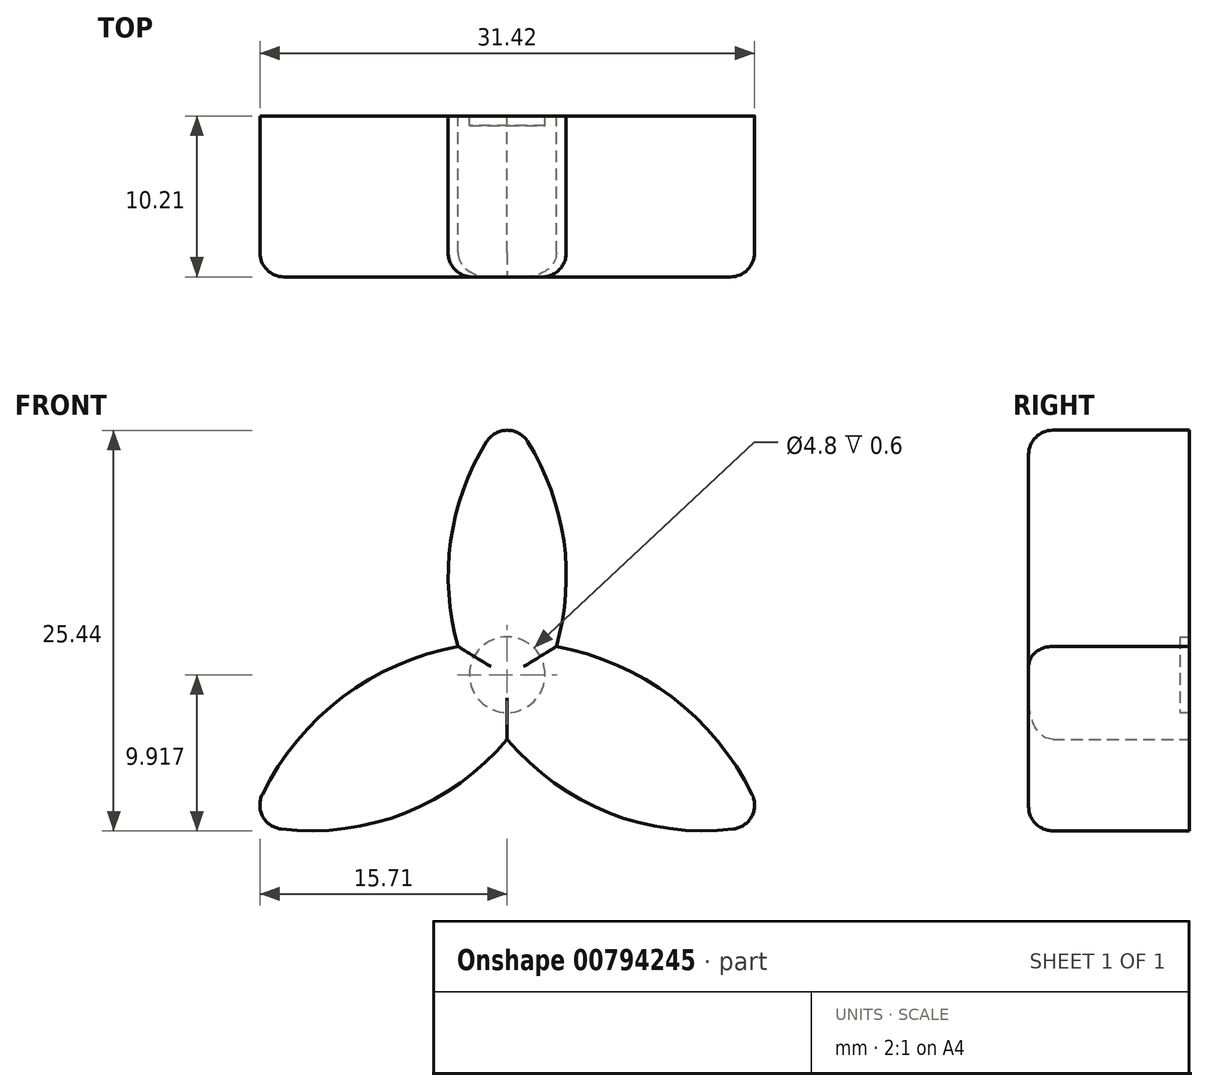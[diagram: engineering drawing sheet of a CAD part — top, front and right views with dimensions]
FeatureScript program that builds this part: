
annotation { "Feature Type Name" : "Feature", "Feature Type Description" : "" }
export const myFeature = defineFeature(function(context is Context, id is Id, definition is map)
    precondition{}
    {
        {
            var Q0;
            Q0=qCreatedBy(makeId("Front.planeOp"),FACE);
            var sketch = newSketch(context, id + "F0", { "sketchPlane" : qUnion([Q0])});
            skLineSegment(sketch, "E0", {"start": v(-12.42, 0) * mm, "end": v(0, 0) * mm});
            skLineSegment(sketch, "E1", {"start": v(0, 0) * mm, "end": v(12.42, 0) * mm});
            skLineSegment(sketch, "E2", {"start": v(0, 0) * mm, "end": v(0, -21.51) * mm});
            skLineSegment(sketch, "E3", {"start": v(-12.42, 0) * mm, "end": v(0, -21.51) * mm});
            skLineSegment(sketch, "E4", {"start": v(12.42, 0) * mm, "end": v(0, -21.51) * mm});
            skCircle(sketch, "E5", {"center": v(-12.42, 0) * mm, "radius": 16.17 * mm});
            skCircle(sketch, "E6", {"center": v(0, -21.51) * mm, "radius": 17.34 * mm});
            skCircle(sketch, "E7", {"center": v(12.42, 0) * mm, "radius": 16.17 * mm});
            skSolve(sketch);
        }
        {
            var Q0;
            {var subQ0=sQuery(id+"F0.wireOp",EDGE,"E6");var subQ1=sQuery(id+"F0.wireOp",EDGE,"E3");var subQ2=makeQuery(id+"F0.imprint","INTERSECT",VERTEX,{"derivedFrom":[subQ1,subQ0]});Q0=makeQuery(id+"F0.imprint","IMPRINT",FACE,{"disambiguationData":[TD([[makeQuery(id+"F0.imprint","IMPRINT",EDGE,{"disambiguationData":[TD([[subQ2,-1.0]])],"derivedFrom":subQ1}),-1.0]])]});}
            var Q1;
            {var subQ0=sQuery(id+"F0.wireOp",EDGE,"E6");var subQ1=sQuery(id+"F0.wireOp",EDGE,"E4");var subQ2=makeQuery(id+"F0.imprint","INTERSECT",VERTEX,{"derivedFrom":[subQ1,subQ0]});Q1=makeQuery(id+"F0.imprint","IMPRINT",FACE,{"disambiguationData":[TD([[makeQuery(id+"F0.imprint","IMPRINT",EDGE,{"disambiguationData":[TD([[subQ2,-1.0]])],"derivedFrom":subQ1}),1.0]])]});}
            var Q2;
            {var subQ0=sQuery(id+"F0.wireOp",EDGE,"E6");var subQ1=sQuery(id+"F0.wireOp",EDGE,"E3");var subQ2=makeQuery(id+"F0.imprint","INTERSECT",VERTEX,{"derivedFrom":[subQ1,subQ0]});Q2=makeQuery(id+"F0.imprint","IMPRINT",FACE,{"disambiguationData":[TD([[makeQuery(id+"F0.imprint","IMPRINT",EDGE,{"disambiguationData":[TD([[subQ2,-1.0]])],"derivedFrom":subQ1}),1.0]])]});}
            var Q3;
            {var subQ0=sQuery(id+"F0.wireOp",EDGE,"E6");var subQ1=sQuery(id+"F0.wireOp",EDGE,"E2");var subQ2=makeQuery(id+"F0.imprint","INTERSECT",VERTEX,{"derivedFrom":[subQ1,subQ0]});Q3=makeQuery(id+"F0.imprint","IMPRINT",FACE,{"disambiguationData":[TD([[makeQuery(id+"F0.imprint","IMPRINT",EDGE,{"disambiguationData":[TD([[subQ2,1.0]])],"derivedFrom":subQ0}),1.0]])]});}
            var Q4;
            {var subQ0=sQuery(id+"F0.wireOp",EDGE,"E6");var subQ1=sQuery(id+"F0.wireOp",EDGE,"E4");var subQ2=makeQuery(id+"F0.imprint","INTERSECT",VERTEX,{"derivedFrom":[subQ1,subQ0]});Q4=makeQuery(id+"F0.imprint","IMPRINT",FACE,{"disambiguationData":[TD([[makeQuery(id+"F0.imprint","IMPRINT",EDGE,{"disambiguationData":[TD([[subQ2,-1.0]])],"derivedFrom":subQ1}),-1.0]])]});}
            var Q5;
            {var subQ0=sQuery(id+"F0.wireOp",EDGE,"E6");var subQ1=sQuery(id+"F0.wireOp",EDGE,"E2");var subQ2=makeQuery(id+"F0.imprint","INTERSECT",VERTEX,{"derivedFrom":[subQ1,subQ0]});Q5=makeQuery(id+"F0.imprint","IMPRINT",FACE,{"disambiguationData":[TD([[makeQuery(id+"F0.imprint","IMPRINT",EDGE,{"disambiguationData":[TD([[subQ2,-1.0]])],"derivedFrom":subQ0}),1.0]])]});}
            var Q6;
            {var subQ0=sQuery(id+"F0.wireOp",EDGE,"E2");var subQ5=sQuery(id+"F0.wireOp",EDGE,"E6");var subQ6=makeQuery(id+"F0.imprint","INTERSECT",VERTEX,{"derivedFrom":[subQ0,subQ5]});Q6=makeQuery(id+"F0.imprint","IMPRINT",FACE,{"disambiguationData":[TD([[makeQuery(id+"F0.imprint","IMPRINT",EDGE,{"disambiguationData":[TD([[subQ6,-1.0]])],"derivedFrom":subQ5}),-1.0]])]});}
            var Q7;
            {var subQ1=sQuery(id+"F0.wireOp",EDGE,"E1");var subQ3=sQuery(id+"F0.wireOp",EDGE,"E5");var subQ4=makeQuery(id+"F0.imprint","INTERSECT",VERTEX,{"derivedFrom":[subQ1,subQ3]});Q7=makeQuery(id+"F0.imprint","IMPRINT",FACE,{"disambiguationData":[TD([[makeQuery(id+"F0.imprint","IMPRINT",EDGE,{"disambiguationData":[TD([[subQ4,1.0]])],"derivedFrom":subQ3}),1.0]])]});}
            var Q8;
            {var subQ3=sQuery(id+"F0.wireOp",EDGE,"E7");var subQ5=sQuery(id+"F0.wireOp",EDGE,"E5");var subQ6=makeQuery(id+"F0.imprint","INTERSECT",VERTEX,{"derivedFrom":[subQ5,subQ3]});Q8=makeQuery(id+"F0.imprint","IMPRINT",FACE,{"disambiguationData":[TD([[makeQuery(id+"F0.imprint","IMPRINT",EDGE,{"disambiguationData":[TD([[subQ6,1.0]])],"derivedFrom":subQ5}),1.0]])]});}
            extrude(context, id + "F1", {"entities" : qUnion([Q0, Q1, Q2, Q3, Q4, Q5, Q6, Q7, Q8]), "depth" : 19.91 * mm, "offsetDistance" : 25.4 * mm});
        }
        {
            var Q0;
            {var subQ0=sQuery(id+"F0.wireOp",EDGE,"E5");var subQ1=makeQuery(id+"F0.imprint","INTERSECT",VERTEX,{"derivedFrom":[sQuery(id+"F0.wireOp",EDGE,"E3"),subQ0]});Q0=makeQuery(id+"F1.opExtrude","CAP_EDGE",EDGE,{"disambiguationData":[OSD([subQ0]),TDD([makeQuery(id+"F0.imprint","IMPRINT",EDGE,{"disambiguationData":[TD([[makeQuery(id+"F0.imprint","INTERSECT",VERTEX,{"disambiguationData":[OD(0.0)],"derivedFrom":[subQ0,sQuery(id+"F0.wireOp",EDGE,"E6")]}),-1.0]])],"derivedFrom":subQ0}),makeQuery(id+"F0.imprint","IMPRINT",EDGE,{"disambiguationData":[TD([[subQ1,-1.0]])],"derivedFrom":subQ0})])],"isStart":false});}
            var Q1;
            {var subQ0=sQuery(id+"F0.wireOp",EDGE,"E6");var subQ1=makeQuery(id+"F0.imprint","INTERSECT",VERTEX,{"derivedFrom":[sQuery(id+"F0.wireOp",EDGE,"E3"),subQ0]});Q1=makeQuery(id+"F1.opExtrude","CAP_EDGE",EDGE,{"disambiguationData":[OSD([subQ0]),TDD([makeQuery(id+"F0.imprint","IMPRINT",EDGE,{"disambiguationData":[TD([[subQ1,1.0]])],"derivedFrom":subQ0}),makeQuery(id+"F0.imprint","IMPRINT",EDGE,{"disambiguationData":[TD([[makeQuery(id+"F0.imprint","INTERSECT",VERTEX,{"disambiguationData":[OD(0.0)],"derivedFrom":[sQuery(id+"F0.wireOp",EDGE,"E5"),subQ0]}),1.0]])],"derivedFrom":subQ0})])],"isStart":false});}
            var Q2;
            {var subQ0=sQuery(id+"F0.wireOp",EDGE,"E7");var subQ1=makeQuery(id+"F0.imprint","INTERSECT",VERTEX,{"derivedFrom":[sQuery(id+"F0.wireOp",EDGE,"E4"),subQ0]});Q2=makeQuery(id+"F1.opExtrude","CAP_EDGE",EDGE,{"disambiguationData":[OSD([subQ0]),TDD([makeQuery(id+"F0.imprint","IMPRINT",EDGE,{"disambiguationData":[TD([[subQ1,1.0]])],"derivedFrom":subQ0}),makeQuery(id+"F0.imprint","IMPRINT",EDGE,{"disambiguationData":[TD([[makeQuery(id+"F0.imprint","INTERSECT",VERTEX,{"disambiguationData":[OD(0.0)],"derivedFrom":[sQuery(id+"F0.wireOp",EDGE,"E6"),subQ0]}),1.0]])],"derivedFrom":subQ0})])],"isStart":false});}
            var Q3;
            {var subQ0=sQuery(id+"F0.wireOp",EDGE,"E6");var subQ1=makeQuery(id+"F0.imprint","INTERSECT",VERTEX,{"derivedFrom":[sQuery(id+"F0.wireOp",EDGE,"E4"),subQ0]});Q3=makeQuery(id+"F1.opExtrude","CAP_EDGE",EDGE,{"disambiguationData":[OSD([subQ0]),TDD([makeQuery(id+"F0.imprint","IMPRINT",EDGE,{"disambiguationData":[TD([[makeQuery(id+"F0.imprint","INTERSECT",VERTEX,{"disambiguationData":[OD(0.0)],"derivedFrom":[subQ0,sQuery(id+"F0.wireOp",EDGE,"E7")]}),-1.0]])],"derivedFrom":subQ0}),makeQuery(id+"F0.imprint","IMPRINT",EDGE,{"disambiguationData":[TD([[subQ1,-1.0]])],"derivedFrom":subQ0})])],"isStart":false});}
            var Q4;
            {var subQ0=sQuery(id+"F0.wireOp",EDGE,"E5");var subQ1=makeQuery(id+"F0.imprint","INTERSECT",VERTEX,{"derivedFrom":[sQuery(id+"F0.wireOp",EDGE,"E1"),subQ0]});Q4=makeQuery(id+"F1.opExtrude","CAP_EDGE",EDGE,{"disambiguationData":[OSD([subQ0]),TDD([makeQuery(id+"F0.imprint","IMPRINT",EDGE,{"disambiguationData":[TD([[makeQuery(id+"F0.imprint","INTERSECT",VERTEX,{"derivedFrom":[subQ0,sQuery(id+"F0.wireOp",EDGE,"E7")]}),1.0]])],"derivedFrom":subQ0}),makeQuery(id+"F0.imprint","IMPRINT",EDGE,{"disambiguationData":[TD([[subQ1,1.0]])],"derivedFrom":subQ0})])],"isStart":false});}
            var Q5;
            {var subQ0=sQuery(id+"F0.wireOp",EDGE,"E7");var subQ1=makeQuery(id+"F0.imprint","INTERSECT",VERTEX,{"derivedFrom":[sQuery(id+"F0.wireOp",EDGE,"E0"),subQ0]});Q5=makeQuery(id+"F1.opExtrude","CAP_EDGE",EDGE,{"disambiguationData":[OSD([subQ0]),TDD([makeQuery(id+"F0.imprint","IMPRINT",EDGE,{"disambiguationData":[TD([[makeQuery(id+"F0.imprint","INTERSECT",VERTEX,{"derivedFrom":[sQuery(id+"F0.wireOp",EDGE,"E5"),subQ0]}),-1.0]])],"derivedFrom":subQ0}),makeQuery(id+"F0.imprint","IMPRINT",EDGE,{"disambiguationData":[TD([[subQ1,-1.0]])],"derivedFrom":subQ0})])],"isStart":false});}
            var Q6;
            {var subQ0=sQuery(id+"F0.wireOp",EDGE,"E7");var subQ1=sQuery(id+"F0.wireOp",EDGE,"E6");Q6=makeQuery(id+"F1.opExtrude","SWEPT_EDGE",EDGE,{"disambiguationData":[OSD([subQ1,subQ0]),TDD([makeQuery(id+"F0.imprint","INTERSECT",VERTEX,{"disambiguationData":[OD(0.0)],"derivedFrom":[subQ1,subQ0]})])]});}
            var Q7;
            Q7=makeQuery(id+"F1.opExtrude","SWEPT_EDGE",EDGE,{"disambiguationData":[OSD([sQuery(id+"F0.wireOp",EDGE,"E5"),sQuery(id+"F0.wireOp",EDGE,"E7")])]});
            var Q8;
            {var subQ0=sQuery(id+"F0.wireOp",EDGE,"E6");var subQ1=sQuery(id+"F0.wireOp",EDGE,"E5");Q8=makeQuery(id+"F1.opExtrude","SWEPT_EDGE",EDGE,{"disambiguationData":[OSD([subQ1,subQ0]),TDD([makeQuery(id+"F0.imprint","INTERSECT",VERTEX,{"disambiguationData":[OD(0.0)],"derivedFrom":[subQ1,subQ0]})])]});}
            fillet(context, id + "F2", {"entities" : qUnion([Q0, Q1, Q2, Q3, Q4, Q5, Q6, Q7, Q8]), "radius" : 1.53 * mm, "tangentPropagation" : true, "allowEdgeOverflow" : false});
        }
        {
            var Q0;
            Q0=makeQuery(id+"F1.opExtrude","CAP_FACE",FACE,{"disambiguationData":[OSD([sQuery(id+"F0.wireOp",EDGE,"E5"),sQuery(id+"F0.wireOp",EDGE,"E6"),sQuery(id+"F0.wireOp",EDGE,"E7")])],"isStart":true});
            extrude(context, id + "F3", {"entities" : qUnion([Q0]), "operationType" : NewBodyOperationType.REMOVE, "oppositeDirection" : true, "depth" : 9.7 * mm, "offsetDistance" : 25 * mm});
        }
        {
            var Q0;
            Q0=makeQuery(id+"F3.boolean.opBoolean","COPY",FACE,{"derivedFrom":makeQuery(id+"F3.opExtrude","CAP_FACE",FACE,{"disambiguationData":[OSD([sQuery(id+"F0.wireOp",EDGE,"E5"),sQuery(id+"F0.wireOp",EDGE,"E6"),sQuery(id+"F0.wireOp",EDGE,"E7")])],"isStart":false})});
            var sketch = newSketch(context, id + "F4", { "sketchPlane" : qUnion([Q0])});
            skCircle(sketch, "E8", {"center": v(0, -6.25) * mm, "radius": 2.4 * mm});
            skSolve(sketch);
        }
        {
            var Q0;
            Q0 = qSketchRegion(id + "F4", true);
            extrude(context, id + "F5", {"entities" : qUnion([Q0]), "operationType" : NewBodyOperationType.REMOVE, "oppositeDirection" : true, "depth" : 0.6 * mm, "offsetDistance" : 25 * mm});
        }
    });
